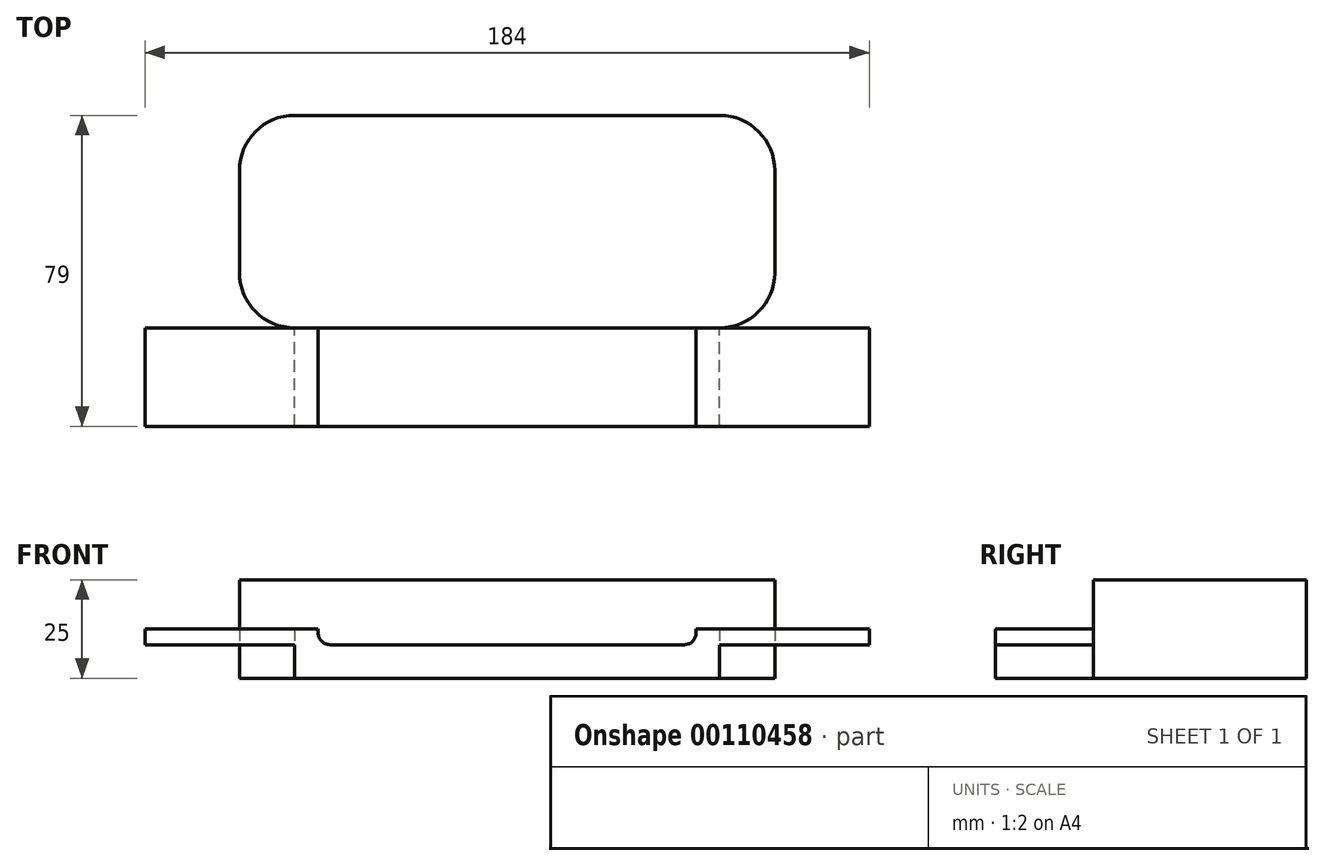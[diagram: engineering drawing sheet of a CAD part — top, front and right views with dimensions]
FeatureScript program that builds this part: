
annotation { "Feature Type Name" : "Feature", "Feature Type Description" : "" }
export const myFeature = defineFeature(function(context is Context, id is Id, definition is map)
    precondition{}
    {
        {
            var Q0;
            Q0=qCreatedBy(makeId("Top.planeOp"),FACE);
            var sketch = newSketch(context, id + "F0", { "sketchPlane" : qUnion([Q0])});
            skLineSegment(sketch, "E0.bottom", {"start": v(-14, 0) * mm, "end": v(-122, 0) * mm});
            skLineSegment(sketch, "E0.top", {"start": v(-14, 54) * mm, "end": v(-122, 54) * mm});
            skLineSegment(sketch, "E0.left", {"start": v(0, 14) * mm, "end": v(0, 40) * mm});
            skLineSegment(sketch, "E0.right", {"start": v(-136, 14) * mm, "end": v(-136, 40) * mm});
            skPoint(sketch, "E1.visualSharp", {"position": v(-136, 54) * mm});
            skArc(sketch, "E1.filletArc", {"start": v(-122, 54) * mm, "mid": v(-131.9, 49.9) * mm, "end": v(-136, 40) * mm});
            skPoint(sketch, "E2.visualSharp", {"position": v(-136, 0) * mm});
            skArc(sketch, "E2.filletArc", {"start": v(-136, 14) * mm, "mid": v(-131.9, 4.1) * mm, "end": v(-122, 0) * mm});
            skPoint(sketch, "E3.visualSharp", {"position": v(0, 0) * mm});
            skArc(sketch, "E3.filletArc", {"start": v(-14, 0) * mm, "mid": v(-4.1, 4.1) * mm, "end": v(0, 14) * mm});
            skPoint(sketch, "E4.visualSharp", {"position": v(0, 54) * mm});
            skArc(sketch, "E4.filletArc", {"start": v(0, 40) * mm, "mid": v(-4.1, 49.9) * mm, "end": v(-14, 54) * mm});
            skSolve(sketch);
        }
        {
            var Q0;
            Q0 = qSketchRegion(id + "F0", true);
            extrude(context, id + "F1", {"entities" : qUnion([Q0]), "endBound" : BoundingType.SYMMETRIC, "depth" : 25 * mm});
        }
        {
            var Q0;
            Q0=makeQuery(id+"F1.opExtrude","CAP_FACE",FACE,{"disambiguationData":[OSD([sQuery(id+"F0.wireOp",EDGE,"E0.bottom"),sQuery(id+"F0.wireOp",EDGE,"E0.top"),sQuery(id+"F0.wireOp",EDGE,"E0.left"),sQuery(id+"F0.wireOp",EDGE,"E0.right"),sQuery(id+"F0.wireOp",EDGE,"E1.filletArc"),sQuery(id+"F0.wireOp",EDGE,"E2.filletArc"),sQuery(id+"F0.wireOp",EDGE,"E3.filletArc"),sQuery(id+"F0.wireOp",EDGE,"E4.filletArc")])],"isStart":false});
            var sketch = newSketch(context, id + "F2", { "sketchPlane" : qUnion([Q0])});
            skLineSegment(sketch, "E5", {"start": v(-122, 54) * mm, "end": v(-122, 0) * mm, "construction": true});
            skLineSegment(sketch, "E6", {"start": v(-14, 54) * mm, "end": v(-14, 0) * mm, "construction": true});
            skLineSegment(sketch, "E7", {"start": v(-94.6, 54) * mm, "end": v(-94.6, 0) * mm});
            skLineSegment(sketch, "E8", {"start": v(-44.4, 54) * mm, "end": v(-44.4, 0) * mm});
            skLineSegment(sketch, "E9", {"start": v(-136, 40) * mm, "end": v(0, 40) * mm, "construction": true});
            skLineSegment(sketch, "E10", {"start": v(-136, 14) * mm, "end": v(0, 14) * mm, "construction": true});
            skCircle(sketch, "E11", {"center": v(-122, 40) * mm, "radius": 7 * mm});
            skCircle(sketch, "E12", {"center": v(-14, 40) * mm, "radius": 7 * mm});
            skCircle(sketch, "E13", {"center": v(-122, 14) * mm, "radius": 7 * mm});
            skCircle(sketch, "E14", {"center": v(-14, 14) * mm, "radius": 7 * mm});
            skSolve(sketch);
        }
        {
            var Q0;
            Q0=sQuery(id+"F2.wireOp",EDGE,"E11");
            var Q1;
            Q1=sQuery(id+"F2.wireOp",EDGE,"E13");
            var Q2;
            Q2=sQuery(id+"F2.wireOp",EDGE,"E14");
            var Q3;
            Q3=sQuery(id+"F2.wireOp",EDGE,"E12");
            extrude(context, id + "F3", {"bodyType" : ToolBodyType.SURFACE, "surfaceEntities" : qUnion([Q0, Q1, Q2, Q3]), "endBound" : BoundingType.SYMMETRIC, "oppositeDirection" : true, "depth" : 25 * mm});
        }
        {
            var Q0;
            Q0=makeQuery(id+"F1.opExtrude","SWEPT_FACE",FACE,{"disambiguationData":[OSD([sQuery(id+"F0.wireOp",EDGE,"E0.bottom")])]});
            var sketch = newSketch(context, id + "F4", { "sketchPlane" : qUnion([Q0])});
            skLineSegment(sketch, "E15", {"start": v(-122, -12.5) * mm, "end": v(-14, -12.5) * mm});
            skLineSegment(sketch, "E16", {"start": v(-14, -12.5) * mm, "end": v(-14, -4) * mm});
            skLineSegment(sketch, "E17", {"start": v(-14, -4) * mm, "end": v(24, -4) * mm});
            skLineSegment(sketch, "E18", {"start": v(24, -4) * mm, "end": v(24, 0) * mm});
            skLineSegment(sketch, "E19", {"start": v(24, 0) * mm, "end": v(-20, 0) * mm});
            skLineSegment(sketch, "E20", {"start": v(-20, 0) * mm, "end": v(-20, -1) * mm});
            skLineSegment(sketch, "E21", {"start": v(-23, -4) * mm, "end": v(-113, -4) * mm});
            skLineSegment(sketch, "E22", {"start": v(-116, -1) * mm, "end": v(-116, 0) * mm});
            skLineSegment(sketch, "E23", {"start": v(-116, 0) * mm, "end": v(-160, 0) * mm});
            skLineSegment(sketch, "E24", {"start": v(-160, 0) * mm, "end": v(-160, -4) * mm});
            skLineSegment(sketch, "E25", {"start": v(-160, -4) * mm, "end": v(-122, -4) * mm});
            skLineSegment(sketch, "E26", {"start": v(-122, -4) * mm, "end": v(-122, -12.5) * mm});
            skPoint(sketch, "E27.visualSharp", {"position": v(-116, -4) * mm});
            skArc(sketch, "E27.filletArc", {"start": v(-116, -1) * mm, "mid": v(-115.12, -3.12) * mm, "end": v(-113, -4) * mm});
            skPoint(sketch, "E28.visualSharp", {"position": v(-20, -4) * mm});
            skArc(sketch, "E28.filletArc", {"start": v(-23, -4) * mm, "mid": v(-20.88, -3.12) * mm, "end": v(-20, -1) * mm});
            skSolve(sketch);
        }
        {
            var Q0;
            Q0 = qSketchRegion(id + "F4", true);
            extrude(context, id + "F5", {"entities" : qUnion([Q0]), "operationType" : NewBodyOperationType.ADD, "depth" : 25 * mm});
        }
    });
